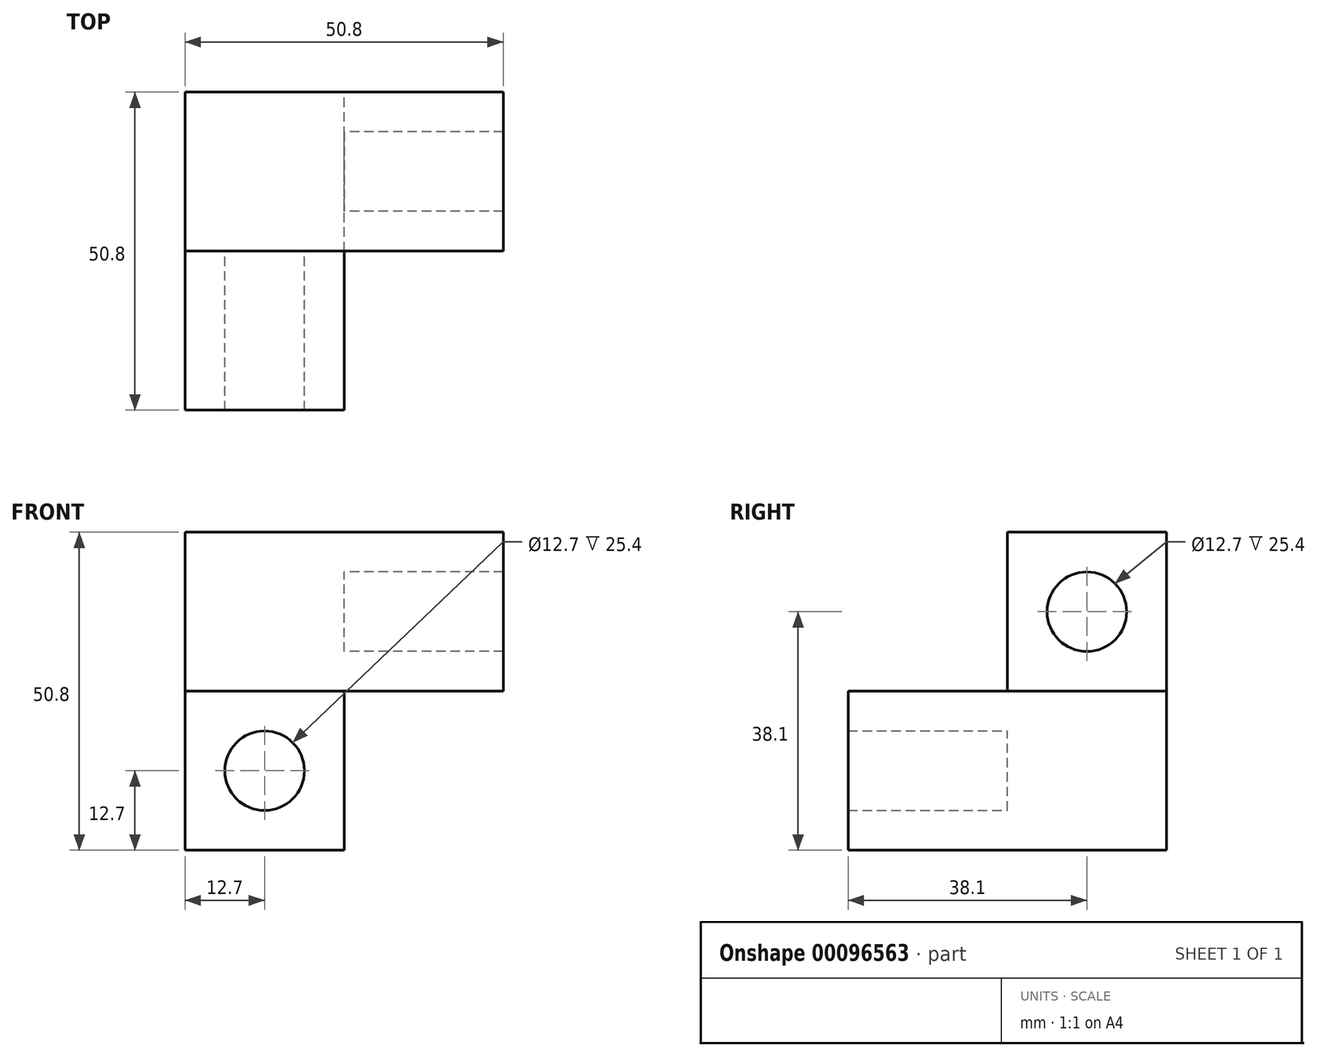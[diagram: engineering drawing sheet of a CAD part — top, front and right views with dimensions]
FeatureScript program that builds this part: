
annotation { "Feature Type Name" : "Feature", "Feature Type Description" : "" }
export const myFeature = defineFeature(function(context is Context, id is Id, definition is map)
    precondition{}
    {
        {
            var Q0;
            Q0=qCreatedBy(makeId("Front.planeOp"),FACE);
            var sketch = newSketch(context, id + "F0", { "sketchPlane" : qUnion([Q0])});
            skLineSegment(sketch, "E0.bottom", {"start": v(12.7, -25.4) * mm, "end": v(-12.7, -25.4) * mm});
            skLineSegment(sketch, "E0.top", {"start": v(12.7, 25.4) * mm, "end": v(-12.7, 25.4) * mm});
            skLineSegment(sketch, "E0.left", {"start": v(12.7, -25.4) * mm, "end": v(12.7, 25.4) * mm});
            skLineSegment(sketch, "E0.right", {"start": v(-12.7, -25.4) * mm, "end": v(-12.7, 25.4) * mm});
            skPoint(sketch, "E0.middle", {"position": v(0, 0) * mm});
            skSolve(sketch);
        }
        {
            var Q0;
            Q0 = qSketchRegion(id + "F0", true);
            extrude(context, id + "F1", {"entities" : qUnion([Q0]), "depth" : 25.4 * mm, "symmetric" : true});
        }
        {
            var Q0;
            Q0=makeQuery(id+"F1.opExtrude","CAP_FACE",FACE,{"disambiguationData":[OSD([sQuery(id+"F0.wireOp",EDGE,"E0.bottom"),sQuery(id+"F0.wireOp",EDGE,"E0.top"),sQuery(id+"F0.wireOp",EDGE,"E0.left"),sQuery(id+"F0.wireOp",EDGE,"E0.right")])],"isStart":false});
            var sketch = newSketch(context, id + "F2", { "sketchPlane" : qUnion([Q0])});
            skLineSegment(sketch, "E1", {"start": v(0, -25.4) * mm, "end": v(0, 0) * mm, "construction": true});
            skLineSegment(sketch, "E2.bottom", {"start": v(-12.7, 0) * mm, "end": v(12.7, 0) * mm});
            skLineSegment(sketch, "E2.top", {"start": v(-12.7, -25.4) * mm, "end": v(12.7, -25.4) * mm});
            skLineSegment(sketch, "E2.left", {"start": v(-12.7, 0) * mm, "end": v(-12.7, -25.4) * mm});
            skLineSegment(sketch, "E2.right", {"start": v(12.7, 0) * mm, "end": v(12.7, -25.4) * mm});
            skLineSegment(sketch, "E3", {"start": v(-12.7, -12.7) * mm, "end": v(12.7, -12.7) * mm, "construction": true});
            skCircle(sketch, "E4", {"center": v(0, -12.7) * mm, "radius": 6.35 * mm});
            skSolve(sketch);
        }
        {
            var Q0;
            Q0=makeQuery(id+"F1.opExtrude","SWEPT_FACE",FACE,{"disambiguationData":[OSD([sQuery(id+"F0.wireOp",EDGE,"E0.left")])]});
            var sketch = newSketch(context, id + "F3", { "sketchPlane" : qUnion([Q0])});
            skLineSegment(sketch, "E5.bottom", {"start": v(-12.7, 25.4) * mm, "end": v(12.7, 25.4) * mm});
            skLineSegment(sketch, "E5.top", {"start": v(-12.7, 0) * mm, "end": v(12.7, 0) * mm});
            skLineSegment(sketch, "E5.left", {"start": v(-12.7, 25.4) * mm, "end": v(-12.7, 0) * mm});
            skLineSegment(sketch, "E5.right", {"start": v(12.7, 25.4) * mm, "end": v(12.7, 0) * mm});
            skLineSegment(sketch, "E6", {"start": v(0, 0) * mm, "end": v(0, 25.4) * mm, "construction": true});
            skLineSegment(sketch, "E7", {"start": v(-12.7, 12.7) * mm, "end": v(12.7, 12.7) * mm, "construction": true});
            skCircle(sketch, "E8", {"center": v(0, 12.7) * mm, "radius": 6.35 * mm});
            skSolve(sketch);
        }
        {
            var Q0;
            Q0 = qSketchRegion(id + "F3", true);
            extrude(context, id + "F4", {"entities" : qUnion([Q0]), "operationType" : NewBodyOperationType.ADD, "depth" : 25.4 * mm});
        }
        {
            var Q0;
            Q0 = qSketchRegion(id + "F2", true);
            extrude(context, id + "F5", {"entities" : qUnion([Q0]), "operationType" : NewBodyOperationType.ADD, "depth" : 25.4 * mm});
        }
    });
